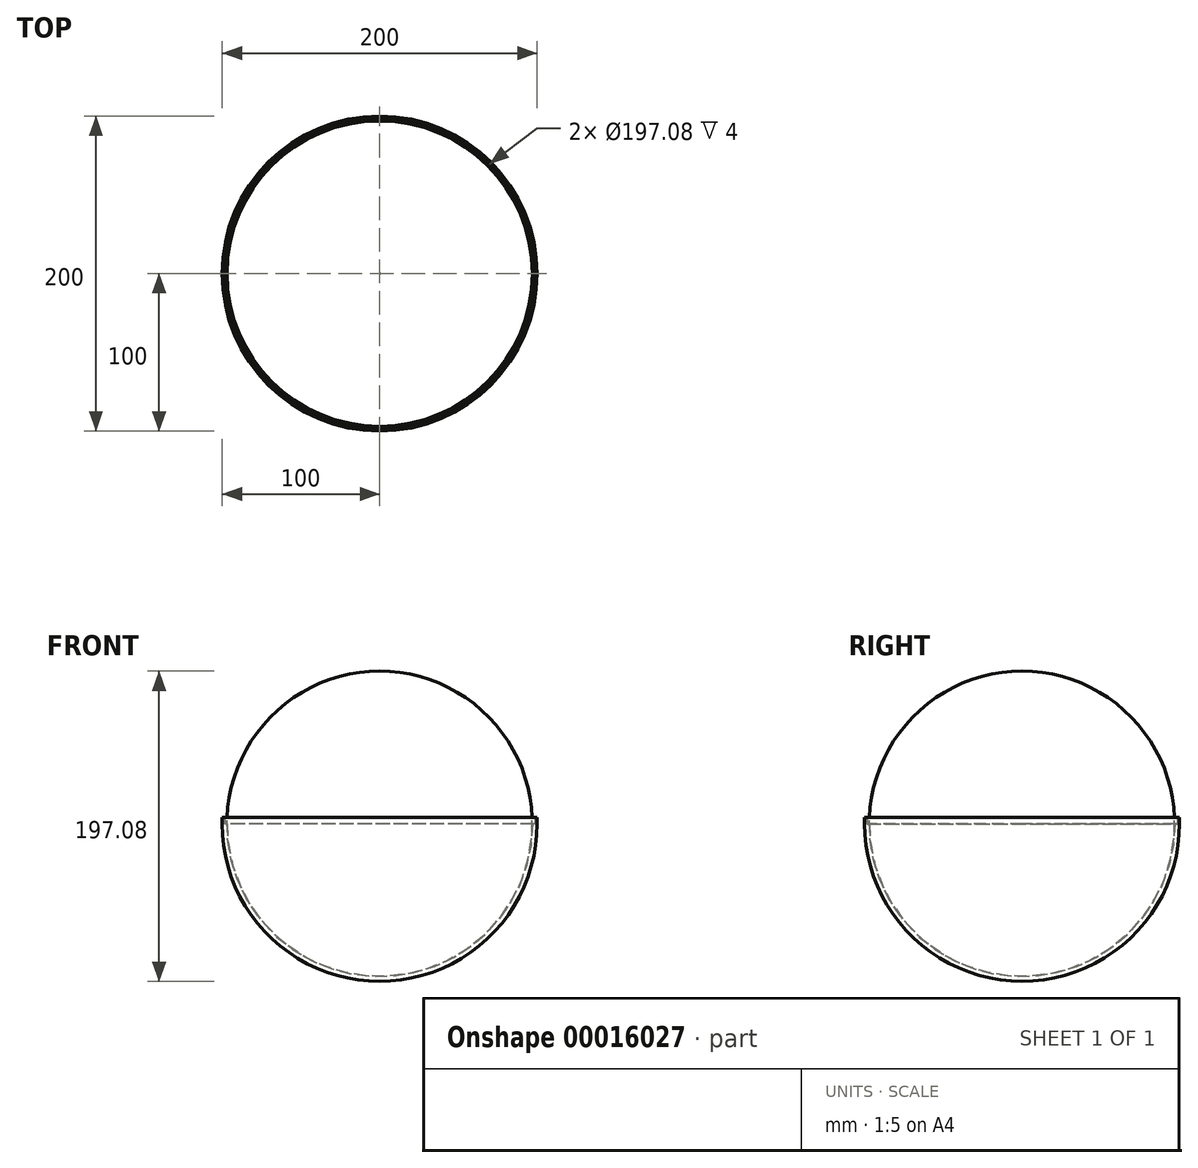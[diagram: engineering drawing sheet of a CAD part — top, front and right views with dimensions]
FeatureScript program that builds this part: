
annotation { "Feature Type Name" : "Feature", "Feature Type Description" : "" }
export const myFeature = defineFeature(function(context is Context, id is Id, definition is map)
    precondition{}
    {
        {
            var Q0;
            Q0=qCreatedBy(makeId("Front.planeOp"),FACE);
            var sketch = newSketch(context, id + "F0", { "sketchPlane" : qUnion([Q0])});
            skLineSegment(sketch, "E0", {"start": v(0, 0) * mm, "end": v(0, 100) * mm, "construction": true});
            skArc(sketch, "E1", {"start": v(0, -100) * mm, "mid": v(70.71, -70.71) * mm, "end": v(100, 0) * mm});
            skArc(sketch, "E2", {"start": v(0, -96.92) * mm, "mid": v(68.56, -68.54) * mm, "end": v(97, 0) * mm});
            skLineSegment(sketch, "E3", {"start": v(0, -96.92) * mm, "end": v(0, -100) * mm});
            skPoint(sketch, "E4.orphan", {"position": v(-97, 0) * mm});
            skPoint(sketch, "E5.orphan", {"position": v(-100, 0) * mm});
            skLineSegment(sketch, "E6", {"start": v(98.54, 0) * mm, "end": v(98.54, 4) * mm});
            skLineSegment(sketch, "E7", {"start": v(100, 0) * mm, "end": v(100, 4) * mm});
            skLineSegment(sketch, "E8", {"start": v(100, 4) * mm, "end": v(98.54, 4) * mm});
            skLineSegment(sketch, "E9", {"start": v(97, 0) * mm, "end": v(98.54, 0) * mm});
            skPoint(sketch, "E10.start.orphan", {"position": v(97, 4) * mm});
            skSolve(sketch);
        }
        {
            var Q0;
            Q0=makeQuery(id+"F0.imprint","IMPRINT",FACE,{"disambiguationData":[TD([[makeQuery(id+"F0.imprint","IMPRINT",EDGE,{"derivedFrom":sQuery(id+"F0.wireOp",EDGE,"E1")}),1.0]])]});
            var Q1;
            Q1=sQuery(id+"F0.wireOp",EDGE,"E0");
            revolve(context, id + "F1", {"entities" : qUnion([Q0]), "axis" : qUnion([Q1]), "revolveType" : RevolveType.FULL});
        }
        {
            var Q0;
            Q0=makeQuery(id+"F1.opRevolve","SWEPT_BODY",BODY,{"disambiguationData":[OSD([sQuery(id+"F0.wireOp",EDGE,"E1"),sQuery(id+"F0.wireOp",EDGE,"E2"),sQuery(id+"F0.wireOp",EDGE,"E3"),sQuery(id+"F0.wireOp",EDGE,"6c113a55-5ab0-4337-85d5-fb513c8c861d"),sQuery(id+"F0.wireOp",EDGE,"E6"),sQuery(id+"F0.wireOp",EDGE,"c5491150-1df0-47e2-a9ed-e175a7e60f0a"),sQuery(id+"F0.wireOp",EDGE,"E10")])]});
            var Q1;
            Q1=makeQuery(id+"F1.opRevolve","SWEPT_FACE",FACE,{"disambiguationData":[OSD([sQuery(id+"F0.wireOp",EDGE,"E1")])]});
            transform(context, id + "F2", {"entities" : qUnion([Q0]), "transformType" : TransformType.ROTATION, "transformAxis" : qUnion([Q1]), "angle" : 180 * degree, "makeCopy" : true});
        }
    });
